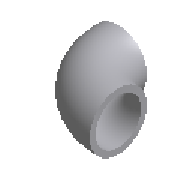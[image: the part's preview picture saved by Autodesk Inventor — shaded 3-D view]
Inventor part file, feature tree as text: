
AUTODESK INVENTOR PART (.ipt)
format: ipt  version: 2023.2 (Build 272271030, 271C)  size: 190,464 bytes
history: native  units: mm (DEFAULTED — no unit token found)
features: other x4, sketch x2, sweep x1
ambient origin geometry x8: Origin, YZ Plane, XZ Plane, XY Plane, X Axis, Y Axis, Z Axis, Center Point
bodies: Solid1 (feature_tree)
feature tree (7):
  sweep  "Sweep1"
  other  "Work Point1"
  other  "Work Axis1"
  other  "Work Point2"
  other  "Work Axis2"
  sketch  "Sketch1"  dims[d0=390.6mm d1=406.4mm]
  sketch  "Sketch2"  dims[d2=406.4mm d3=90.0deg d4=406.4mm d5=0.0mm d6=0.0mm]
